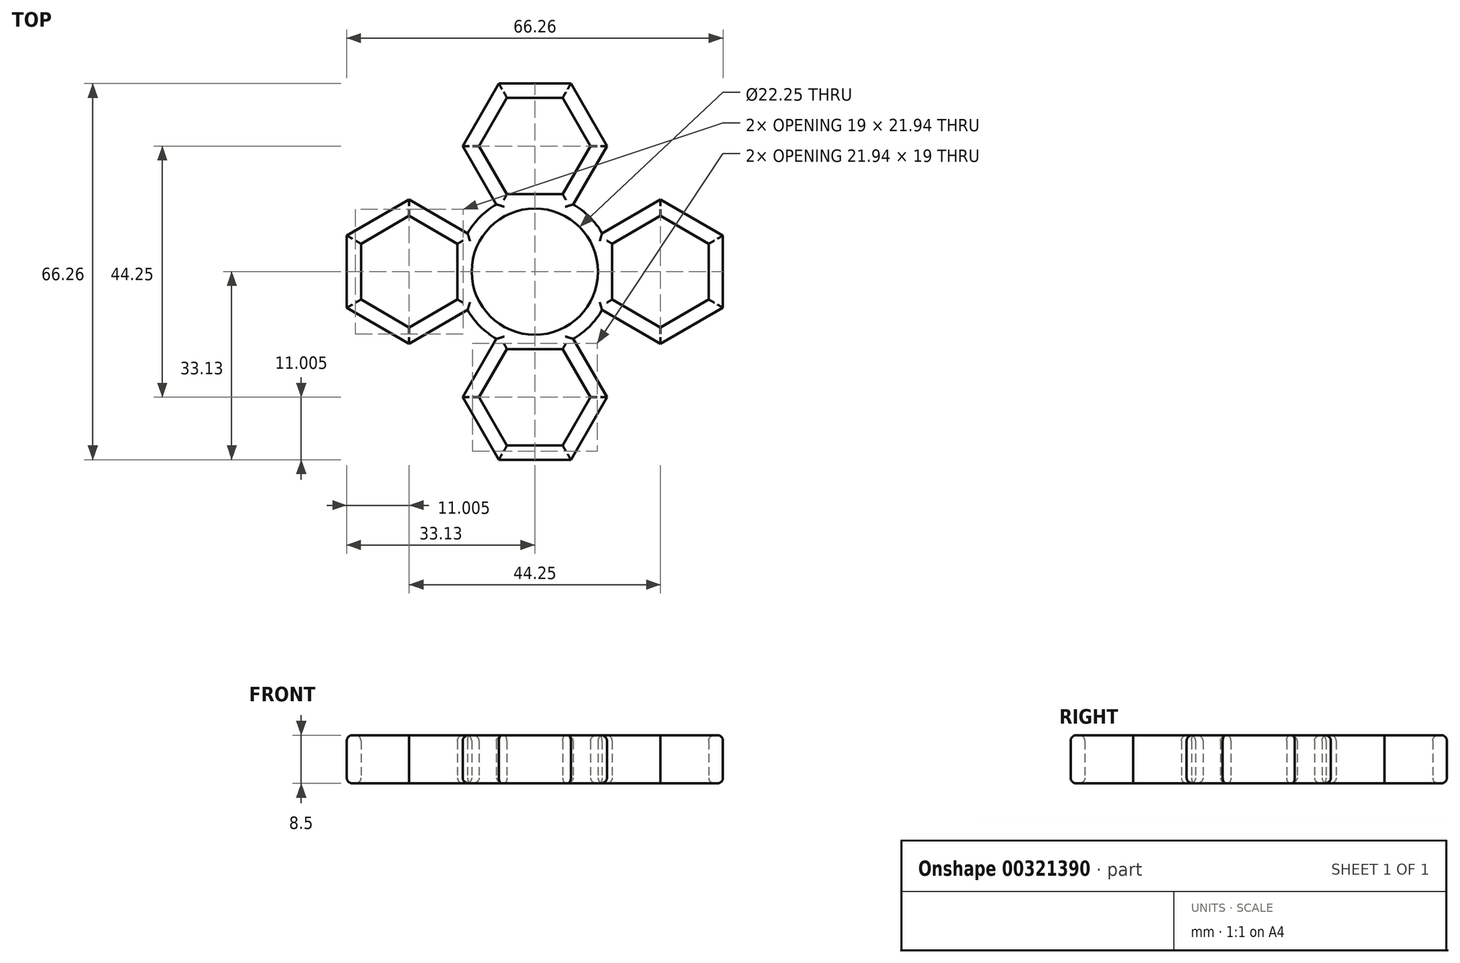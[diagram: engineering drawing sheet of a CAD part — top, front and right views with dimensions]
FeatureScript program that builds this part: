
annotation { "Feature Type Name" : "Feature", "Feature Type Description" : "" }
export const myFeature = defineFeature(function(context is Context, id is Id, definition is map)
    precondition{}
    {
        {
            var Q0;
            Q0=qCreatedBy(makeId("Top.planeOp"),FACE);
            var sketch = newSketch(context, id + "F0", { "sketchPlane" : qUnion([Q0])});
            skCircle(sketch, "E0", {"center": v(0, 0) * mm, "radius": 11.12 * mm});
            skCircle(sketch, "E1", {"center": v(0, 0) * mm, "radius": 13.62 * mm});
            skPoint(sketch, "E2", {"position": v(0, 11.12) * mm});
            skPoint(sketch, "E3", {"position": v(0, 13.62) * mm});
            skLineSegment(sketch, "E4", {"start": v(0, 13.62) * mm, "end": v(0, 22.12) * mm, "construction": true});
            skCircle(sketch, "E5.cCircle", {"center": v(0, 22.12) * mm, "radius": 11 * mm, "construction": true});
            skLineSegment(sketch, "E5.0", {"start": v(6.35, 11.12) * mm, "end": v(-6.35, 11.12) * mm});
            skLineSegment(sketch, "E5.1", {"start": v(-6.35, 11.12) * mm, "end": v(-12.7, 22.12) * mm});
            skLineSegment(sketch, "E5.2", {"start": v(-12.7, 22.12) * mm, "end": v(-6.35, 33.12) * mm});
            skLineSegment(sketch, "E5.3", {"start": v(-6.35, 33.12) * mm, "end": v(6.35, 33.12) * mm});
            skLineSegment(sketch, "E5.4", {"start": v(6.35, 33.12) * mm, "end": v(12.7, 22.13) * mm});
            skLineSegment(sketch, "E5.5", {"start": v(12.7, 22.13) * mm, "end": v(6.35, 11.12) * mm});
            skCircle(sketch, "E6.cCircle", {"center": v(0, 22.12) * mm, "radius": 8.5 * mm, "construction": true});
            skLineSegment(sketch, "E6.0", {"start": v(4.9, 13.62) * mm, "end": v(-4.9, 13.62) * mm});
            skLineSegment(sketch, "E6.1", {"start": v(-4.9, 13.62) * mm, "end": v(-9.81, 22.12) * mm});
            skLineSegment(sketch, "E6.2", {"start": v(-9.81, 22.12) * mm, "end": v(-4.9, 30.62) * mm});
            skLineSegment(sketch, "E6.3", {"start": v(-4.9, 30.62) * mm, "end": v(4.9, 30.62) * mm});
            skLineSegment(sketch, "E6.4", {"start": v(4.9, 30.62) * mm, "end": v(9.81, 22.13) * mm});
            skLineSegment(sketch, "E6.5", {"start": v(9.81, 22.13) * mm, "end": v(4.9, 13.62) * mm});
            skLineSegment(sketch, "E7.1.0", {"start": v(-22.13, 12.7) * mm, "end": v(-11.12, 6.35) * mm});
            skCircle(sketch, "E7.1.1", {"center": v(-22.12, 0) * mm, "radius": 8.5 * mm, "construction": true});
            skLineSegment(sketch, "E7.1.2", {"start": v(-30.62, 4.9) * mm, "end": v(-22.13, 9.81) * mm});
            skLineSegment(sketch, "E7.1.3", {"start": v(-30.62, -4.9) * mm, "end": v(-30.62, 4.9) * mm});
            skLineSegment(sketch, "E7.1.4", {"start": v(-33.12, -6.35) * mm, "end": v(-33.12, 6.35) * mm});
            skLineSegment(sketch, "E7.1.5", {"start": v(-22.13, 9.81) * mm, "end": v(-13.62, 4.9) * mm});
            skCircle(sketch, "E7.1.6", {"center": v(-22.12, 0) * mm, "radius": 11 * mm, "construction": true});
            skLineSegment(sketch, "E7.1.7", {"start": v(-22.12, -12.7) * mm, "end": v(-33.12, -6.35) * mm});
            skLineSegment(sketch, "E7.1.8", {"start": v(-22.12, -9.81) * mm, "end": v(-30.62, -4.9) * mm});
            skLineSegment(sketch, "E7.1.9", {"start": v(-13.62, -4.9) * mm, "end": v(-22.12, -9.81) * mm});
            skLineSegment(sketch, "E7.1.10", {"start": v(-11.12, -6.35) * mm, "end": v(-22.12, -12.7) * mm});
            skLineSegment(sketch, "E7.1.11", {"start": v(-13.62, 4.9) * mm, "end": v(-13.62, -4.9) * mm});
            skLineSegment(sketch, "E7.1.12", {"start": v(-11.12, 6.35) * mm, "end": v(-11.12, -6.35) * mm});
            skLineSegment(sketch, "E7.1.13", {"start": v(-33.12, 6.35) * mm, "end": v(-22.13, 12.7) * mm});
            skLineSegment(sketch, "E7.2.0", {"start": v(-12.7, -22.13) * mm, "end": v(-6.35, -11.12) * mm});
            skCircle(sketch, "E7.2.1", {"center": v(0, -22.12) * mm, "radius": 8.5 * mm, "construction": true});
            skLineSegment(sketch, "E7.2.2", {"start": v(-4.9, -30.62) * mm, "end": v(-9.81, -22.13) * mm});
            skLineSegment(sketch, "E7.2.3", {"start": v(4.9, -30.62) * mm, "end": v(-4.9, -30.63) * mm});
            skLineSegment(sketch, "E7.2.4", {"start": v(6.35, -33.12) * mm, "end": v(-6.35, -33.12) * mm});
            skLineSegment(sketch, "E7.2.5", {"start": v(-9.81, -22.13) * mm, "end": v(-4.9, -13.62) * mm});
            skCircle(sketch, "E7.2.6", {"center": v(0, -22.12) * mm, "radius": 11 * mm, "construction": true});
            skLineSegment(sketch, "E7.2.7", {"start": v(12.7, -22.12) * mm, "end": v(6.35, -33.12) * mm});
            skLineSegment(sketch, "E7.2.8", {"start": v(9.81, -22.12) * mm, "end": v(4.9, -30.62) * mm});
            skLineSegment(sketch, "E7.2.9", {"start": v(4.9, -13.63) * mm, "end": v(9.81, -22.12) * mm});
            skLineSegment(sketch, "E7.2.10", {"start": v(6.35, -11.13) * mm, "end": v(12.7, -22.12) * mm});
            skLineSegment(sketch, "E7.2.11", {"start": v(-4.9, -13.62) * mm, "end": v(4.9, -13.62) * mm});
            skLineSegment(sketch, "E7.2.12", {"start": v(-6.35, -11.12) * mm, "end": v(6.35, -11.13) * mm});
            skLineSegment(sketch, "E7.2.13", {"start": v(-6.35, -33.12) * mm, "end": v(-12.7, -22.13) * mm});
            skLineSegment(sketch, "E8.2.3.0", {"start": v(22.13, -12.7) * mm, "end": v(11.12, -6.35) * mm});
            skCircle(sketch, "E8.3.3.0", {"center": v(22.12, 0) * mm, "radius": 8.5 * mm, "construction": true});
            skLineSegment(sketch, "E8.5.3.0", {"start": v(30.62, -4.9) * mm, "end": v(22.13, -9.81) * mm});
            skLineSegment(sketch, "E8.8.3.0", {"start": v(30.62, 4.9) * mm, "end": v(30.62, -4.9) * mm});
            skLineSegment(sketch, "E8.11.3.0", {"start": v(33.12, 6.35) * mm, "end": v(33.12, -6.35) * mm});
            skLineSegment(sketch, "E8.14.3.0", {"start": v(22.13, -9.81) * mm, "end": v(13.62, -4.9) * mm});
            skCircle(sketch, "E8.17.3.0", {"center": v(22.12, 0) * mm, "radius": 11 * mm, "construction": true});
            skLineSegment(sketch, "E8.19.3.0", {"start": v(22.12, 12.7) * mm, "end": v(33.12, 6.35) * mm});
            skLineSegment(sketch, "E8.22.3.0", {"start": v(22.12, 9.81) * mm, "end": v(30.62, 4.9) * mm});
            skLineSegment(sketch, "E8.25.3.0", {"start": v(13.63, 4.9) * mm, "end": v(22.13, 9.81) * mm});
            skLineSegment(sketch, "E8.28.3.0", {"start": v(11.13, 6.35) * mm, "end": v(22.13, 12.7) * mm});
            skLineSegment(sketch, "E8.31.3.0", {"start": v(13.62, -4.9) * mm, "end": v(13.63, 4.9) * mm});
            skLineSegment(sketch, "E8.34.3.0", {"start": v(11.12, -6.35) * mm, "end": v(11.13, 6.35) * mm});
            skLineSegment(sketch, "E8.37.3.0", {"start": v(33.12, -6.35) * mm, "end": v(22.13, -12.7) * mm});
            skSolve(sketch);
        }
        {
            var Q0;
            Q0 = qSketchRegion(id + "F0", true);
            extrude(context, id + "F1", {"entities" : qUnion([Q0]), "depth" : 8.5 * mm});
        }
        {
            var Q0;
            Q0=makeQuery(id+"F1.opExtrude","CAP_FACE",FACE,{"disambiguationData":[OSD([sQuery(id+"F0.wireOp",EDGE,"E0"),sQuery(id+"F0.wireOp",EDGE,"E1"),sQuery(id+"F0.wireOp",EDGE,"ddadf6dc-f5d2-4cd8-abd3-9a1c2dd37bdf.0"),sQuery(id+"F0.wireOp",EDGE,"ddadf6dc-f5d2-4cd8-abd3-9a1c2dd37bdf.1"),sQuery(id+"F0.wireOp",EDGE,"ddadf6dc-f5d2-4cd8-abd3-9a1c2dd37bdf.2"),sQuery(id+"F0.wireOp",EDGE,"ddadf6dc-f5d2-4cd8-abd3-9a1c2dd37bdf.3"),sQuery(id+"F0.wireOp",EDGE,"ddadf6dc-f5d2-4cd8-abd3-9a1c2dd37bdf.4"),sQuery(id+"F0.wireOp",EDGE,"ddadf6dc-f5d2-4cd8-abd3-9a1c2dd37bdf.5"),sQuery(id+"F0.wireOp",EDGE,"5241ff82-7c5c-424e-8f4c-5420cca2d40c.1"),sQuery(id+"F0.wireOp",EDGE,"5241ff82-7c5c-424e-8f4c-5420cca2d40c.2"),sQuery(id+"F0.wireOp",EDGE,"5241ff82-7c5c-424e-8f4c-5420cca2d40c.3"),sQuery(id+"F0.wireOp",EDGE,"5241ff82-7c5c-424e-8f4c-5420cca2d40c.4"),sQuery(id+"F0.wireOp",EDGE,"5241ff82-7c5c-424e-8f4c-5420cca2d40c.5"),sQuery(id+"F0.wireOp",EDGE,"9910855f-52a1-4833-bd6f-27078994df99.1.0"),sQuery(id+"F0.wireOp",EDGE,"9910855f-52a1-4833-bd6f-27078994df99.1.1"),sQuery(id+"F0.wireOp",EDGE,"9910855f-52a1-4833-bd6f-27078994df99.1.2"),sQuery(id+"F0.wireOp",EDGE,"9910855f-52a1-4833-bd6f-27078994df99.1.3"),sQuery(id+"F0.wireOp",EDGE,"9910855f-52a1-4833-bd6f-27078994df99.1.4"),sQuery(id+"F0.wireOp",EDGE,"9910855f-52a1-4833-bd6f-27078994df99.1.5"),sQuery(id+"F0.wireOp",EDGE,"9910855f-52a1-4833-bd6f-27078994df99.1.6"),sQuery(id+"F0.wireOp",EDGE,"9910855f-52a1-4833-bd6f-27078994df99.1.8"),sQuery(id+"F0.wireOp",EDGE,"9910855f-52a1-4833-bd6f-27078994df99.1.9"),sQuery(id+"F0.wireOp",EDGE,"9910855f-52a1-4833-bd6f-27078994df99.1.10"),sQuery(id+"F0.wireOp",EDGE,"9910855f-52a1-4833-bd6f-27078994df99.1.13"),sQuery(id+"F0.wireOp",EDGE,"9910855f-52a1-4833-bd6f-27078994df99.2.0"),sQuery(id+"F0.wireOp",EDGE,"9910855f-52a1-4833-bd6f-27078994df99.2.1"),sQuery(id+"F0.wireOp",EDGE,"9910855f-52a1-4833-bd6f-27078994df99.2.2"),sQuery(id+"F0.wireOp",EDGE,"9910855f-52a1-4833-bd6f-27078994df99.2.3"),sQuery(id+"F0.wireOp",EDGE,"9910855f-52a1-4833-bd6f-27078994df99.2.4"),sQuery(id+"F0.wireOp",EDGE,"9910855f-52a1-4833-bd6f-27078994df99.2.5"),sQuery(id+"F0.wireOp",EDGE,"9910855f-52a1-4833-bd6f-27078994df99.2.6"),sQuery(id+"F0.wireOp",EDGE,"9910855f-52a1-4833-bd6f-27078994df99.2.8"),sQuery(id+"F0.wireOp",EDGE,"9910855f-52a1-4833-bd6f-27078994df99.2.9"),sQuery(id+"F0.wireOp",EDGE,"9910855f-52a1-4833-bd6f-27078994df99.2.10"),sQuery(id+"F0.wireOp",EDGE,"9910855f-52a1-4833-bd6f-27078994df99.2.13"),sQuery(id+"F0.wireOp",EDGE,"e2d9fed3-6ae2-467a-8839-64efe0a2e874.3.3.0"),sQuery(id+"F0.wireOp",EDGE,"e2d9fed3-6ae2-467a-8839-64efe0a2e874.6.3.0"),sQuery(id+"F0.wireOp",EDGE,"e2d9fed3-6ae2-467a-8839-64efe0a2e874.9.3.0"),sQuery(id+"F0.wireOp",EDGE,"e2d9fed3-6ae2-467a-8839-64efe0a2e874.12.3.0"),sQuery(id+"F0.wireOp",EDGE,"e2d9fed3-6ae2-467a-8839-64efe0a2e874.15.3.0"),sQuery(id+"F0.wireOp",EDGE,"e2d9fed3-6ae2-467a-8839-64efe0a2e874.16.3.0"),sQuery(id+"F0.wireOp",EDGE,"e2d9fed3-6ae2-467a-8839-64efe0a2e874.18.3.0"),sQuery(id+"F0.wireOp",EDGE,"e2d9fed3-6ae2-467a-8839-64efe0a2e874.23.3.0"),sQuery(id+"F0.wireOp",EDGE,"e2d9fed3-6ae2-467a-8839-64efe0a2e874.26.3.0"),sQuery(id+"F0.wireOp",EDGE,"e2d9fed3-6ae2-467a-8839-64efe0a2e874.29.3.0"),sQuery(id+"F0.wireOp",EDGE,"e2d9fed3-6ae2-467a-8839-64efe0a2e874.35.3.0")])],"isStart":true});
            var Q1;
            Q1=makeQuery(id+"F1.opExtrude","CAP_FACE",FACE,{"disambiguationData":[OSD([sQuery(id+"F0.wireOp",EDGE,"E0"),sQuery(id+"F0.wireOp",EDGE,"E1"),sQuery(id+"F0.wireOp",EDGE,"ddadf6dc-f5d2-4cd8-abd3-9a1c2dd37bdf.0"),sQuery(id+"F0.wireOp",EDGE,"ddadf6dc-f5d2-4cd8-abd3-9a1c2dd37bdf.1"),sQuery(id+"F0.wireOp",EDGE,"ddadf6dc-f5d2-4cd8-abd3-9a1c2dd37bdf.2"),sQuery(id+"F0.wireOp",EDGE,"ddadf6dc-f5d2-4cd8-abd3-9a1c2dd37bdf.3"),sQuery(id+"F0.wireOp",EDGE,"ddadf6dc-f5d2-4cd8-abd3-9a1c2dd37bdf.4"),sQuery(id+"F0.wireOp",EDGE,"ddadf6dc-f5d2-4cd8-abd3-9a1c2dd37bdf.5"),sQuery(id+"F0.wireOp",EDGE,"5241ff82-7c5c-424e-8f4c-5420cca2d40c.1"),sQuery(id+"F0.wireOp",EDGE,"5241ff82-7c5c-424e-8f4c-5420cca2d40c.2"),sQuery(id+"F0.wireOp",EDGE,"5241ff82-7c5c-424e-8f4c-5420cca2d40c.3"),sQuery(id+"F0.wireOp",EDGE,"5241ff82-7c5c-424e-8f4c-5420cca2d40c.4"),sQuery(id+"F0.wireOp",EDGE,"5241ff82-7c5c-424e-8f4c-5420cca2d40c.5"),sQuery(id+"F0.wireOp",EDGE,"9910855f-52a1-4833-bd6f-27078994df99.1.0"),sQuery(id+"F0.wireOp",EDGE,"9910855f-52a1-4833-bd6f-27078994df99.1.1"),sQuery(id+"F0.wireOp",EDGE,"9910855f-52a1-4833-bd6f-27078994df99.1.2"),sQuery(id+"F0.wireOp",EDGE,"9910855f-52a1-4833-bd6f-27078994df99.1.3"),sQuery(id+"F0.wireOp",EDGE,"9910855f-52a1-4833-bd6f-27078994df99.1.4"),sQuery(id+"F0.wireOp",EDGE,"9910855f-52a1-4833-bd6f-27078994df99.1.5"),sQuery(id+"F0.wireOp",EDGE,"9910855f-52a1-4833-bd6f-27078994df99.1.6"),sQuery(id+"F0.wireOp",EDGE,"9910855f-52a1-4833-bd6f-27078994df99.1.8"),sQuery(id+"F0.wireOp",EDGE,"9910855f-52a1-4833-bd6f-27078994df99.1.9"),sQuery(id+"F0.wireOp",EDGE,"9910855f-52a1-4833-bd6f-27078994df99.1.10"),sQuery(id+"F0.wireOp",EDGE,"9910855f-52a1-4833-bd6f-27078994df99.1.13"),sQuery(id+"F0.wireOp",EDGE,"9910855f-52a1-4833-bd6f-27078994df99.2.0"),sQuery(id+"F0.wireOp",EDGE,"9910855f-52a1-4833-bd6f-27078994df99.2.1"),sQuery(id+"F0.wireOp",EDGE,"9910855f-52a1-4833-bd6f-27078994df99.2.2"),sQuery(id+"F0.wireOp",EDGE,"9910855f-52a1-4833-bd6f-27078994df99.2.3"),sQuery(id+"F0.wireOp",EDGE,"9910855f-52a1-4833-bd6f-27078994df99.2.4"),sQuery(id+"F0.wireOp",EDGE,"9910855f-52a1-4833-bd6f-27078994df99.2.5"),sQuery(id+"F0.wireOp",EDGE,"9910855f-52a1-4833-bd6f-27078994df99.2.6"),sQuery(id+"F0.wireOp",EDGE,"9910855f-52a1-4833-bd6f-27078994df99.2.8"),sQuery(id+"F0.wireOp",EDGE,"9910855f-52a1-4833-bd6f-27078994df99.2.9"),sQuery(id+"F0.wireOp",EDGE,"9910855f-52a1-4833-bd6f-27078994df99.2.10"),sQuery(id+"F0.wireOp",EDGE,"9910855f-52a1-4833-bd6f-27078994df99.2.13"),sQuery(id+"F0.wireOp",EDGE,"e2d9fed3-6ae2-467a-8839-64efe0a2e874.3.3.0"),sQuery(id+"F0.wireOp",EDGE,"e2d9fed3-6ae2-467a-8839-64efe0a2e874.6.3.0"),sQuery(id+"F0.wireOp",EDGE,"e2d9fed3-6ae2-467a-8839-64efe0a2e874.9.3.0"),sQuery(id+"F0.wireOp",EDGE,"e2d9fed3-6ae2-467a-8839-64efe0a2e874.12.3.0"),sQuery(id+"F0.wireOp",EDGE,"e2d9fed3-6ae2-467a-8839-64efe0a2e874.15.3.0"),sQuery(id+"F0.wireOp",EDGE,"e2d9fed3-6ae2-467a-8839-64efe0a2e874.16.3.0"),sQuery(id+"F0.wireOp",EDGE,"e2d9fed3-6ae2-467a-8839-64efe0a2e874.18.3.0"),sQuery(id+"F0.wireOp",EDGE,"e2d9fed3-6ae2-467a-8839-64efe0a2e874.23.3.0"),sQuery(id+"F0.wireOp",EDGE,"e2d9fed3-6ae2-467a-8839-64efe0a2e874.26.3.0"),sQuery(id+"F0.wireOp",EDGE,"e2d9fed3-6ae2-467a-8839-64efe0a2e874.29.3.0"),sQuery(id+"F0.wireOp",EDGE,"e2d9fed3-6ae2-467a-8839-64efe0a2e874.35.3.0")])],"isStart":false});
            fillet(context, id + "F2", {"entities" : qUnion([Q0, Q1]), "radius" : 1 * mm, "tangentPropagation" : true, "allowEdgeOverflow" : false});
        }
    });
